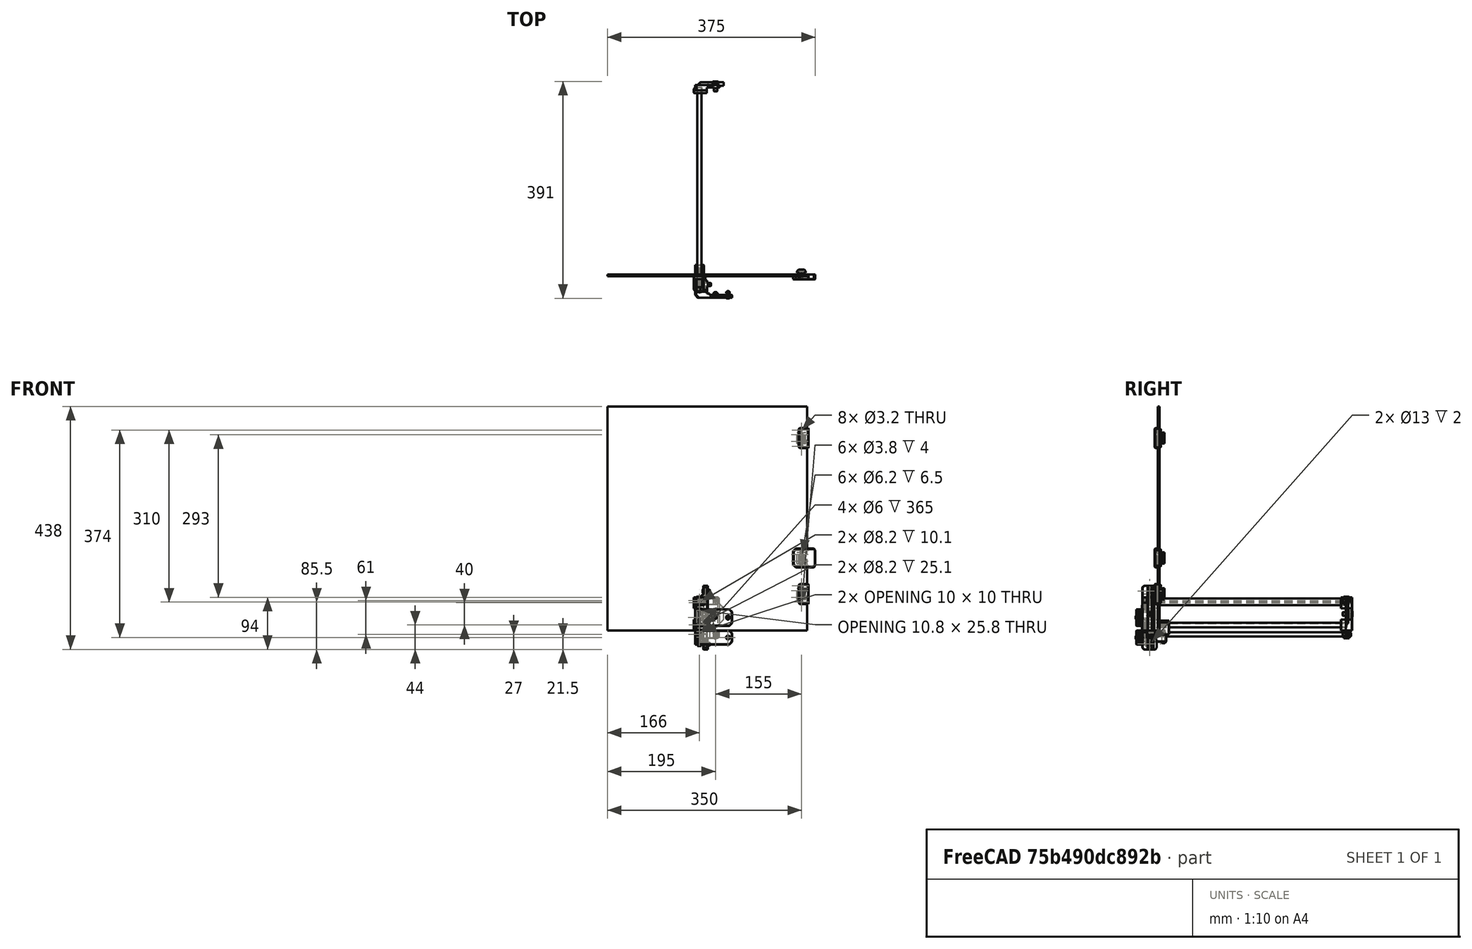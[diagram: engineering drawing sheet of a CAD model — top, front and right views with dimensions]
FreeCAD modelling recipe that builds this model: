
FCSTD DOCUMENT  (FreeCAD 0.19R24291 (Git))
Label: front-panel-assembly
License: All rights reserved
LicenseURL: http://en.wikipedia.org/wiki/All_rights_reserved
objects: Part::FeaturePython×29, Part::Feature×21, App::Part×3, Part::Cylinder×2, Part::Box×1
note: 53 computed .brp shape members not serialized (recipe doc carries the construction recipe); baked Part::Feature solids carry a one-line shape summary decoded from their .brp

FEATURE [Part::Box] Box  label="panel-360x404x3mm"
  AttacherType = Attacher::AttachEngine3D
  Height = 404
  Length = 360
  Placement = pos=(-180,0,0) rot=(0,0,1;0rad)
  Width = 3
FEATURE [Part::Feature] Cut010011008009003016002  label="tube-8x365mm001"
  shape: bbox 8 x 365 x 8 mm, 4 faces (baked)
FEATURE [Part::Feature] Cut010011008009003016003  label="hingle-base002"
  Placement = pos=(-28,0,0) rot=(0,0,1;0rad)
  shape: bbox 16 x 40 x 13 mm, 28 faces (baked)
FEATURE [Part::Cylinder] Cylinder016023002  label="magnet-6x3mm004"
  Angle = 360
  AttacherType = Attacher::AttachEngine3D
  Height = 3
  Placement = pos=(-21,-19,15) rot=(0,-1,0;1.5708rad)
  Radius = 3
FEATURE [Part::FeaturePython] Screw007  label="M6x12-Screw"  # Fasteners workbench fastener (typed FeaturePython)
  Placement = pos=(15,345,30) rot=(-1,0,0;1.5708rad)
  diameter = 7
  invert = true
  length = 14
  lengthCustom = 12
  matchOuter = true
  offset = 0
  thread = false
  type = 33
FEATURE [Part::FeaturePython] Screw008  label="M6x15-Screw"  # Fasteners workbench fastener (typed FeaturePython)
  Placement = pos=(-8,-15,30) rot=(0,-1,0;1.5708rad)
  diameter = 4
  invert = true
  length = 13
  lengthCustom = 15
  matchOuter = true
  offset = 0
  thread = false
  type = 39
FEATURE [Part::FeaturePython] Washer006  label="M3-Washer022"  # Fasteners workbench fastener (typed FeaturePython)
  Placement = pos=(15,-31,-12.5) rot=(1,0,0;1.5708rad)
  diameter = 4
  invert = false
  matchOuter = true
  offset = -3
  type = 5
FEATURE [Part::FeaturePython] Screw009  label="M3x6-Screw022"  # Fasteners workbench fastener (typed FeaturePython)
  Placement = pos=(15,-31,-12.5) rot=(-1,0,0;1.5708rad)
  baseObject = -> Washer006 [Edge5]
  diameter = 1
  invert = true
  length = 0
  lengthCustom = 6
  matchOuter = true
  offset = 0
  thread = false
  type = 39
FEATURE [Part::FeaturePython] Screw010  label="M3x10-Screw"  # Fasteners workbench fastener (typed FeaturePython)
  Placement = pos=(37.5,-37,-12.5) rot=(1,0,0;1.5708rad)
  diameter = 4
  invert = false
  length = 3
  lengthCustom = 10
  matchOuter = true
  offset = 0
  thread = false
  type = 33
FEATURE [Part::FeaturePython] Washer007  label="M3-Washer023"  # Fasteners workbench fastener (typed FeaturePython)
  Placement = pos=(37.5,-31,-12.5) rot=(-1,0,0;1.5708rad)
  diameter = 4
  invert = true
  matchOuter = true
  offset = 3
  type = 5
FEATURE [Part::FeaturePython] Nut  label="M3-Nut"  # Fasteners workbench fastener (typed FeaturePython)
  Placement = pos=(37.5,-30.45,-12.5) rot=(-1,0,0;1.5708rad)
  baseObject = -> Washer007 [Edge1]
  diameter = 4
  invert = false
  matchOuter = true
  offset = 0
  thread = false
  type = 7
FEATURE [Part::FeaturePython] Screw012  label="M5x20-Screw"  # Fasteners workbench fastener (typed FeaturePython)
  Placement = pos=(-14,10,-20) rot=(1,0,0;3.14159rad)
  baseObject = -> Cut010011008009003016003 [Edge31]
  diameter = 3
  invert = true
  length = 5
  lengthCustom = 20
  matchOuter = true
  offset = 0
  thread = false
  type = 39
FEATURE [Part::FeaturePython] Screw013  label="M3x25-Screw"  # Fasteners workbench fastener (typed FeaturePython)
  Placement = pos=(-14,-20,-25) rot=(1,0,0;3.14159rad)
  diameter = 4
  invert = false
  length = 8
  lengthCustom = 25
  matchOuter = true
  offset = 0
  thread = false
  type = 33
FEATURE [Part::Feature] Cut010011008009001  label="magnet-nut001"
  Placement = pos=(170,4,56) rot=(0,0,1;0rad)
  shape: bbox 16 x 7.5 x 20 mm, 17 faces (baked)
FEATURE [Part::Feature] Cut010011008009003016004  label="magnet-nut002"
  Placement = pos=(170,4,121) rot=(0,0,1;0rad)
  shape: bbox 16 x 7.5 x 20 mm, 17 faces (baked)
FEATURE [Part::Feature] Cut010011008009003016005  label="magnet-nut003"
  Placement = pos=(170,4,337) rot=(0,0,1;0rad)
  shape: bbox 16 x 7.5 x 20 mm, 17 faces (baked)
FEATURE [Part::Feature] Chamfer016016008004017002013001  label="door-hanlde-sm-mag001"
  Placement = pos=(185,4,114) rot=(0,0,1;0rad)
  shape: bbox 40 x 9 x 34 mm, 29 faces (baked)
FEATURE [Part::Cylinder] Cylinder016023003  label="magnet-6x3mm005"
  Angle = 360
  AttacherType = Attacher::AttachEngine3D
  Height = 3
  Placement = pos=(-21,-19,5) rot=(0,-1,0;1.5708rad)
  Radius = 3
FEATURE [Part::Feature] Chamfer016016008004017002013005001  label="dock-magnet-mounter001"
  Placement = pos=(185,4,48) rot=(0,0,1;0rad)
  shape: bbox 18 x 9 x 36 mm, 29 faces (baked)
FEATURE [Part::Feature] Chamfer016016008004017002013005002  label="dock-magnet-mounter002"
  Placement = pos=(185,4,329) rot=(0,0,1;0rad)
  shape: bbox 18 x 9 x 36 mm, 29 faces (baked)
FEATURE [Part::FeaturePython] Washer  label="M3-Washer"  # Fasteners workbench fastener (typed FeaturePython)
  Placement = pos=(170,3,361.5) rot=(-1,0,0;1.5708rad)
  baseObject = -> Chamfer016016008004017002013005002 [Edge30]
  diameter = 4
  invert = false
  matchOuter = true
  offset = 3
  type = 5
FEATURE [Part::FeaturePython] Washer008  label="M3-Washer016"  # Fasteners workbench fastener (typed FeaturePython)
  Placement = pos=(170,3,332.5) rot=(-1,0,0;1.5708rad)
  baseObject = -> Chamfer016016008004017002013005002 [Edge25]
  diameter = 4
  invert = false
  matchOuter = true
  offset = 3
  type = 5
FEATURE [Part::FeaturePython] Washer009  label="M3-Washer018"  # Fasteners workbench fastener (typed FeaturePython)
  Placement = pos=(170,3,80.5) rot=(-1,0,0;1.5708rad)
  baseObject = -> Chamfer016016008004017002013005001 [Edge30]
  diameter = 4
  invert = false
  matchOuter = true
  offset = 3
  type = 5
FEATURE [Part::FeaturePython] Washer010  label="M3-Washer017"  # Fasteners workbench fastener (typed FeaturePython)
  Placement = pos=(170,3,51.5) rot=(-1,0,0;1.5708rad)
  baseObject = -> Chamfer016016008004017002013005001 [Edge25]
  diameter = 4
  invert = false
  matchOuter = true
  offset = 3
  type = 5
FEATURE [Part::FeaturePython] Washer011  label="M3-Washer021"  # Fasteners workbench fastener (typed FeaturePython)
  Placement = pos=(170,3,144.5) rot=(-1,0,0;1.5708rad)
  baseObject = -> Chamfer016016008004017002013001 [Edge52]
  diameter = 4
  invert = false
  matchOuter = true
  offset = 3
  type = 5
FEATURE [Part::FeaturePython] Washer012  label="M3-Washer020"  # Fasteners workbench fastener (typed FeaturePython)
  Placement = pos=(170,3,117.5) rot=(-1,0,0;1.5708rad)
  baseObject = -> Chamfer016016008004017002013001 [Edge47]
  diameter = 4
  invert = false
  matchOuter = true
  offset = 3
  type = 5
FEATURE [Part::FeaturePython] Screw  label="M3x6-Screw"  # Fasteners workbench fastener (typed FeaturePython)
  Placement = pos=(170,3.55,361.5) rot=(-1,0,0;1.5708rad)
  baseObject = -> Washer [Edge1]
  diameter = 1
  invert = false
  length = 0
  lengthCustom = 6
  matchOuter = true
  offset = 0
  thread = false
  type = 39
FEATURE [Part::FeaturePython] Screw014  label="M3x6-Screw017"  # Fasteners workbench fastener (typed FeaturePython)
  Placement = pos=(170,3.55,332.5) rot=(-1,0,0;1.5708rad)
  baseObject = -> Washer008 [Edge1]
  diameter = 1
  invert = false
  length = 0
  lengthCustom = 6
  matchOuter = true
  offset = 0
  thread = false
  type = 39
FEATURE [Part::FeaturePython] Screw015  label="M3x6-Screw018"  # Fasteners workbench fastener (typed FeaturePython)
  Placement = pos=(170,3.55,144.5) rot=(-1,0,0;1.5708rad)
  baseObject = -> Washer011 [Edge1]
  diameter = 1
  invert = false
  length = 0
  lengthCustom = 6
  matchOuter = true
  offset = 0
  thread = false
  type = 39
FEATURE [Part::FeaturePython] Screw016  label="M3x6-Screw019"  # Fasteners workbench fastener (typed FeaturePython)
  Placement = pos=(170,3.55,117.5) rot=(-1,0,0;1.5708rad)
  baseObject = -> Washer012 [Edge1]
  diameter = 1
  invert = false
  length = 0
  lengthCustom = 6
  matchOuter = true
  offset = 0
  thread = false
  type = 39
FEATURE [Part::FeaturePython] Screw017  label="M3x6-Screw020"  # Fasteners workbench fastener (typed FeaturePython)
  Placement = pos=(170,3.55,80.5) rot=(-1,0,0;1.5708rad)
  baseObject = -> Washer009 [Edge1]
  diameter = 1
  invert = false
  length = 0
  lengthCustom = 6
  matchOuter = true
  offset = 0
  thread = false
  type = 39
FEATURE [Part::FeaturePython] Screw018  label="M3x6-Screw021"  # Fasteners workbench fastener (typed FeaturePython)
  Placement = pos=(170,3.55,51.5) rot=(-1,0,0;1.5708rad)
  baseObject = -> Washer010 [Edge1]
  diameter = 1
  invert = false
  length = 0
  lengthCustom = 6
  matchOuter = true
  offset = 0
  thread = false
  type = 39
FEATURE [App::Part] Part001  label="door-panel"
  Group = -> [Box,Cut010011008009001,Cut010011008009003016004,Cut010011008009003016005,Chamfer016016008004017002013001,Chamfer016016008004017002013005001,Chamfer016016008004017002013005002,Washer008,Washer,Washer010,Washer009,Washer012,Washer011,Screw014,Screw,Screw016,Screw015,Screw018,Screw017]
  Origin = -> Origin001
  Placement = pos=(185,-34,0) rot=(0,0,1;0rad)
FEATURE [Part::Feature] Chamfer016016008004017002013005004001
  Placement = pos=(0,0,0) rot=(0,1,0;3.14159rad)
  shape: bbox 67 x 24 x 25 mm, 71 faces (baked)
FEATURE [Part::Feature] Fusion018002  label="slider003"
  Placement = pos=(-14,2e-15,10) rot=(-1,0,0;1.5708rad)
  shape: bbox 16 x 20 x 25 mm, 76 faces (baked)
FEATURE [Part::Feature] Chamfer016016008004017002013005004015001
  Placement = pos=(9.4e-14,340,0) rot=(0,0,1;3.14159rad)
  shape: bbox 54 x 20 x 60 mm, 72 faces (baked)
FEATURE [Part::Feature] Cut010011008009003016006  label="tube-8x365mm002"
  Placement = pos=(0,0,40) rot=(0,0,1;0rad)
  shape: bbox 8 x 365 x 8 mm, 4 faces (baked)
FEATURE [Part::Feature] Part__Mirroring002002  label="front-rod-mount-dual"
  Placement = pos=(-1.6e-14,-30,0) rot=(0,0,1;0rad)
  shape: bbox 25 x 28 x 60 mm, 68 faces (baked)
FEATURE [App::Part] Part003  label="door-rail-old"
  Group = -> [Cut010011008009003016003,Fusion018002,Cut010011008009003016002,Cylinder016023002,Screw007,Screw008,Washer006,Screw009,Screw010,Washer007,Nut,Screw012,Screw013,Cylinder016023003,Chamfer016016008004017002013005004001,Chamfer016016008004017002013005004015001,Cut010011008009003016006,Part__Mirroring002002]
  Origin = -> Origin003
  Placement = pos=(0,0,373) rot=(0,0,1;0rad)
FEATURE [Part::Feature] Chamfer006015001001001
  Placement = pos=(0,340,-14) rot=(0,0,1;0rad)
  shape: bbox 44 x 10 x 14 mm, 28 faces (baked)
FEATURE [Part::Feature] Cut010011008009003016026008003008004001
  Placement = pos=(0,-30,0) rot=(0,0,1;0rad)
  shape: bbox 16 x 24 x 75 mm, 188 faces (baked)
FEATURE [Part::Feature] Chamfer006006001
  Placement = pos=(0,-30,0) rot=(0,0,1;0rad)
  shape: bbox 65 x 21 x 30 mm, 53 faces (baked)
FEATURE [Part::Feature] Part__Mirroring002001  label="Chamfer006001 (Mirror #1)002"
  Placement = pos=(0,-30,47) rot=(0,0,1;0rad)
  shape: bbox 23 x 26 x 34 mm, 45 faces (baked)
FEATURE [Part::Feature] Part__Mirroring001001  label="Chamfer006001 (Mirror #2)001"
  Placement = pos=(0,-30,0) rot=(0,0,1;0rad)
  shape: bbox 23 x 26 x 34 mm, 45 faces (baked)
FEATURE [Part::Feature] Cut010011008009003016026008003008004002  label="tube-8x365mm003"
  Placement = pos=(0,0,44) rot=(0,0,1;0rad)
  shape: bbox 8 x 365 x 8 mm, 4 faces (baked)
FEATURE [Part::Feature] Cut010011008009003016026008003008004003  label="tube-8x365mm004"
  Placement = pos=(0,0,-17) rot=(0,0,1;0rad)
  shape: bbox 8 x 365 x 8 mm, 4 faces (baked)
FEATURE [Part::Feature] Chamfer016016008004017002013005004015002
  Placement = pos=(0,340,47) rot=(0,0,1;0rad)
  shape: bbox 44 x 10 x 14 mm, 28 faces (baked)
FEATURE [Part::FeaturePython] Screw019  label="M3x8-Screw"  # Fasteners workbench fastener (typed FeaturePython)
  Placement = pos=(37.5,-37,23.5) rot=(1,0,0;1.5708rad)
  baseObject = -> Chamfer006006001 [Edge6]
  diameter = 4
  invert = false
  length = 2
  lengthCustom = 8
  matchOuter = true
  offset = 0
  thread = false
  type = 33
FEATURE [Part::FeaturePython] Nut001  label="M3-Nut001"  # Fasteners workbench fastener (typed FeaturePython)
  Placement = pos=(37.5,-31,23.5) rot=(-1,0,0;1.5708rad)
  baseObject = -> Chamfer006006001 [Edge16]
  diameter = 4
  invert = true
  matchOuter = true
  offset = 3
  thread = false
  type = 7
FEATURE [Part::FeaturePython] Screw020  label="M4x8-Screw"  # Fasteners workbench fastener (typed FeaturePython)
  Placement = pos=(15,-31,23.5) rot=(-1,0,0;1.5708rad)
  baseObject = -> Chamfer006006001 [Edge42]
  diameter = 2
  invert = true
  length = 1
  lengthCustom = 8
  matchOuter = true
  offset = 3
  thread = false
  type = 39
FEATURE [Part::FeaturePython] Screw021  label="M6x10-Screw"  # Fasteners workbench fastener (typed FeaturePython)
  Placement = pos=(-5,-15,71) rot=(0,-1,0;1.5708rad)
  baseObject = -> Part__Mirroring002001 [Edge109]
  diameter = 4
  invert = true
  length = 0
  lengthCustom = 10
  matchOuter = true
  offset = 0
  thread = false
  type = 39
FEATURE [Part::FeaturePython] Screw022  label="M6x10-Screw001"  # Fasteners workbench fastener (typed FeaturePython)
  Placement = pos=(-5,-15,-24) rot=(0,-1,0;1.5708rad)
  baseObject = -> Part__Mirroring001001 [Edge109]
  diameter = 4
  invert = false
  length = 0
  lengthCustom = 10
  matchOuter = true
  offset = 0
  thread = false
  type = 39
FEATURE [Part::FeaturePython] Screw023  label="M6x12-Screw001"  # Fasteners workbench fastener (typed FeaturePython)
  Placement = pos=(15,345,-7) rot=(-1,0,0;1.5708rad)
  baseObject = -> Chamfer006015001001001 [Edge32]
  diameter = 4
  invert = true
  length = 1
  lengthCustom = 12
  matchOuter = true
  offset = 0
  thread = false
  type = 39
FEATURE [Part::FeaturePython] Screw024  label="M6x12-Screw002"  # Fasteners workbench fastener (typed FeaturePython)
  Placement = pos=(15,345,54) rot=(-1,0,0;1.5708rad)
  baseObject = -> Chamfer016016008004017002013005004015002 [Edge32]
  diameter = 4
  invert = true
  length = 1
  lengthCustom = 12
  matchOuter = true
  offset = 0
  thread = false
  type = 39
FEATURE [Part::FeaturePython] Screw025  label="M3x1-Screw"  # Fasteners workbench fastener (typed FeaturePython)
  Placement = pos=(-14,-23.5,43) rot=(0,0,1;0rad)
  baseObject = -> Cut010011008009003016026008003008004001 [Edge493]
  diameter = 4
  invert = false
  length = 10
  lengthCustom = 1
  matchOuter = true
  offset = 0
  thread = false
  type = 33
FEATURE [App::Part] Part  label="door-rail"
  Group = -> [Chamfer006015001001001,Cut010011008009003016026008003008004001,Chamfer006006001,Part__Mirroring002001,Part__Mirroring001001,Cut010011008009003016026008003008004002,Cut010011008009003016026008003008004003,Chamfer016016008004017002013005004015002,Screw020,Nut001,Screw019,Screw021,Screw022,Screw023,Screw024,Screw025]
  Origin = -> Origin
